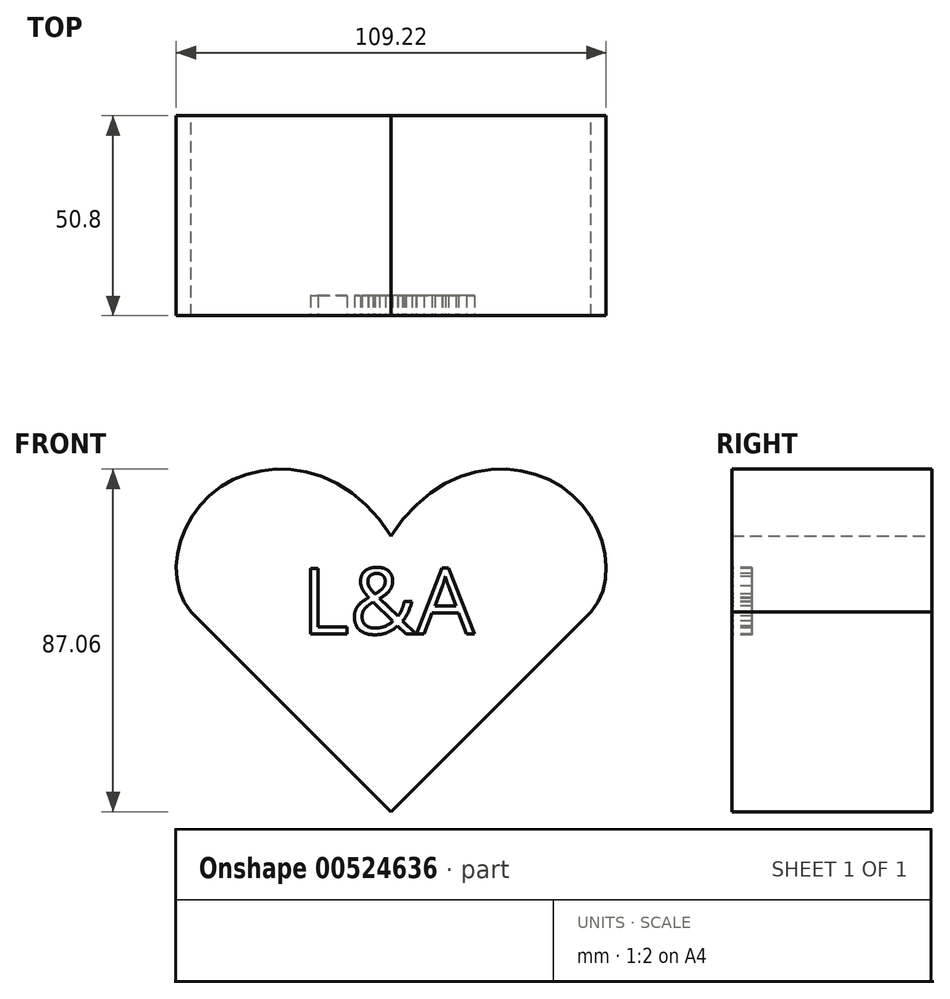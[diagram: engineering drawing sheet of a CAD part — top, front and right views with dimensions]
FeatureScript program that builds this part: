
annotation { "Feature Type Name" : "Feature", "Feature Type Description" : "" }
export const myFeature = defineFeature(function(context is Context, id is Id, definition is map)
    precondition{}
    {
        {
            var Q0;
            Q0=qCreatedBy(makeId("Front.planeOp"),FACE);
            var sketch = newSketch(context, id + "F0", { "sketchPlane" : qUnion([Q0])});
            skLineSegment(sketch, "E0", {"start": v(0, 0) * mm, "end": v(-50.8, 50.8) * mm});
            skLineSegment(sketch, "E1", {"start": v(0, 0) * mm, "end": v(50.8, 50.8) * mm});
            skLineSegment(sketch, "E2", {"start": v(0, 0) * mm, "end": v(0, 109.26) * mm, "construction": true});
            skFitSpline(sketch, "E3", {"points": [v(50.8, 50.8) * mm, v(45.22, 81.17) * mm, v(0, 70.03) * mm], "startDerivative": vector(46.72, 53.14) * mm, "endDerivative": vector(-66.43, -107.63) * mm});
            skFitSpline(sketch, "E4.MirrorCS", {"points": [v(-50.8, 50.8) * mm, v(-45.22, 81.17) * mm, v(0, 70.03) * mm], "startDerivative": vector(-46.72, 53.14) * mm, "endDerivative": vector(66.43, -107.63) * mm});
            skSolve(sketch);
        }
        {
            var Q0;
            Q0=makeQuery(id+"F0.imprint","IMPRINT",FACE,{"disambiguationData":[TD([[makeQuery(id+"F0.imprint","IMPRINT",EDGE,{"derivedFrom":sQuery(id+"F0.wireOp",EDGE,"E0")}),-1.0]])]});
            extrude(context, id + "F1", {"entities" : qUnion([Q0]), "depth" : 50.8 * mm, "offsetDistance" : 25.4 * mm});
        }
        {
            var Q0;
            Q0=makeQuery(id+"F1.opExtrude","CAP_FACE",FACE,{"disambiguationData":[OSD([sQuery(id+"F0.wireOp",EDGE,"E0"),sQuery(id+"F0.wireOp",EDGE,"E1"),sQuery(id+"F0.wireOp",EDGE,"E3"),sQuery(id+"F0.wireOp",EDGE,"E4.MirrorCS")])],"isStart":false});
            var sketch = newSketch(context, id + "F2", { "sketchPlane" : qUnion([Q0])});
            skText(sketch, "E5", { "text": "L&A", "fontName": "OpenSans-Regular.ttf"});
            skLineSegment(sketch, "E6", {"start": v(0, 70.03) * mm, "end": v(0, 0) * mm, "construction": true});
            const initialGuessF2  = {"E5": [-0.02275, 0.04521, 1, 0, 0.0168]};
            skSetInitialGuess(sketch, initialGuessF2);
            skSolve(sketch);
        }
        {
            var Q0;
            Q0 = qSketchRegion(id + "F2", true);
            var Q1;
            Q1 = qConstructionFilter(qBodyType(qCreatedBy(id + "F2" ,EDGE), BodyType.WIRE), ConstructionObject.NO);
            extrude(context, id + "F3", {"entities" : qUnion([Q0]), "operationType" : NewBodyOperationType.REMOVE, "surfaceEntities" : qUnion([Q1]), "oppositeDirection" : true, "depth" : 5.08 * mm, "offsetDistance" : 25.4 * mm});
        }
    });
